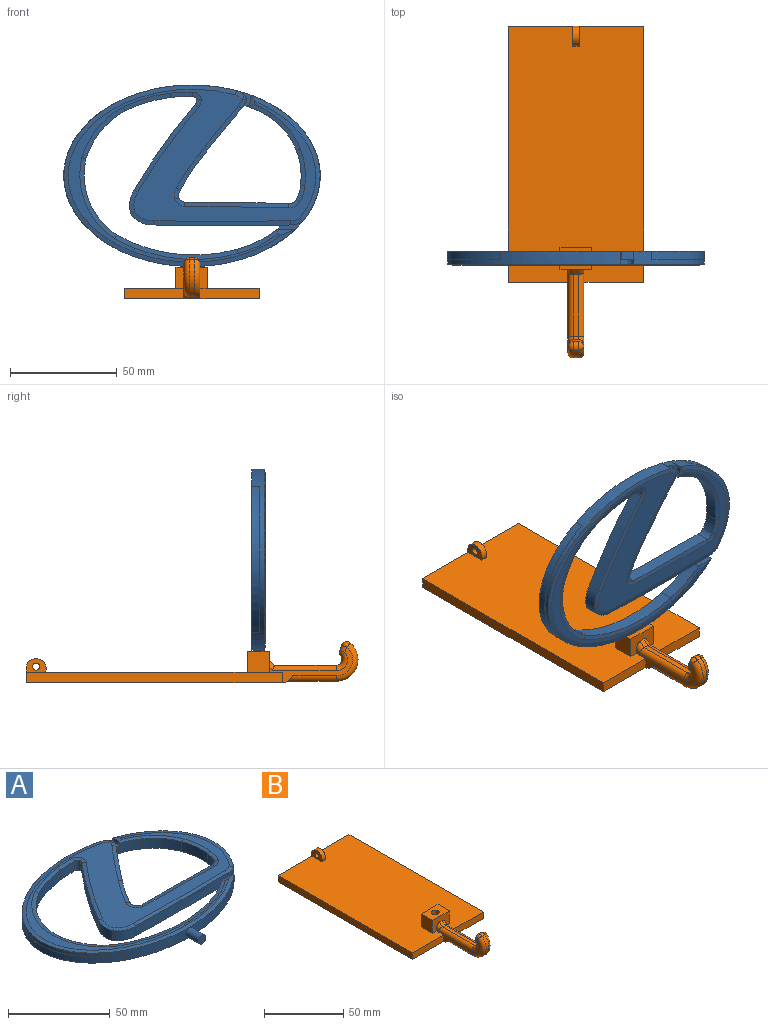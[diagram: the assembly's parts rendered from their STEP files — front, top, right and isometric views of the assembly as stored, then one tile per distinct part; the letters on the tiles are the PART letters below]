
ASSEMBLY  parts=2 mates=1
PART A: 74 faces, bbox 120.8x94.6x6.7 mm
  f0: extruded ~108.39x85.12mm, area 999.4mm2, adj f1,f4,f19,f35,f36,f37,f38,f39
  f1: plane 120.46x85.21mm, normal (0,0,-1), area 3845.7mm2, adj f0,f5,f6,f7,f8,f9,f10,f11
  f2: plane 7.37x6.32mm, normal (0,0,1), area 14.3mm2, adj f3,f17,f18,f19,f25,f34,f71
  f3: cylinder r=2.05mm len=2.18mm, axis (0,0,-1), area 3.9mm2, adj f2,f18,f19,f43
  f4: cylinder r=5144.41mm len=8.58mm, axis (0,0,-1), area 18.7mm2, adj f0,f5,f35,f40
  f5: cylinder r=52.6mm len=18.51mm, axis (0,0,-1), area 124.5mm2, adj f1,f4,f6,f42,f70
  f6: cylinder r=74.66mm len=56.61mm, axis (0,0,-1), area 350.5mm2, adj f1,f5,f7,f44
  f7: cylinder r=33.68mm len=35.7mm, axis (0,0,-1), area 245.3mm2, adj f1,f6,f8,f46
  f8: cylinder r=38.92mm len=22.56mm, axis (0,0,-1), area 178.8mm2, adj f1,f7,f9,f48
  f9: cylinder r=68.86mm len=21.32mm, axis (0,0,-1), area 133.6mm2, adj f1,f8,f10,f50
  f10: cylinder r=70.53mm len=10.22mm, axis (0,0,-1), area 61.4mm2, adj f1,f9,f11,f52
  f11: cylinder r=2.08mm len=5.99mm, axis (0,0,-1), area 17.5mm2, adj f1,f10,f20,f54
  f12: cylinder r=1264.57mm len=63.82mm, axis (0,0,-1), area 365.8mm2, adj f1,f13,f23,f35,f64,f70
  f13: cylinder r=9.39mm len=5.95mm, axis (0,0,-1), area 13.7mm2, adj f12,f24,f35,f66
  f14: cylinder r=33.54mm len=10.41mm, axis (0,0,-1), area 69.3mm2, adj f1,f15,f25,f67,f71
  f15: cylinder r=32.42mm len=15.62mm, axis (0,0,-1), area 122.6mm2, adj f1,f14,f16,f65
  f16: cylinder r=32.25mm len=16.25mm, axis (0,0,-1), area 99.2mm2, adj f1,f15,f26,f63
  f17: cylinder r=10.16mm len=5.99mm, axis (0,0,-1), area 12.1mm2, adj f1,f2,f18,f32,f47,f71
  f18: cylinder r=3.51mm len=2.18mm, axis (0,0,-1), area 3.9mm2, adj f2,f3,f17,f45
  f19: cylinder r=11.51mm len=5.99mm, axis (0,0,-1), area 10.4mm2, adj f0,f1,f2,f3,f34,f41
  f20: cylinder r=2.94mm len=5.99mm, axis (0,0,-1), area 14.2mm2, adj f1,f11,f21,f56
  f21: cylinder r=262.41mm len=39.99mm, axis (0,0,-1), area 294.8mm2, adj f1,f20,f22,f58
  f22: cylinder r=13.1mm len=11.43mm, axis (0,0,-1), area 71.6mm2, adj f1,f21,f23,f60
  f23: cylinder r=12.43mm len=10.87mm, axis (0,0,-1), area 75.2mm2, adj f1,f12,f22,f62
  f24: extruded ~59.5x33.1mm, area 204.1mm2, adj f1,f13,f25,f35,f36,f68
  f25: cylinder r=4.29mm len=5.99mm, axis (0,0,-1), area 13.8mm2, adj f1,f2,f14,f24,f34,f69
  f26: cylinder r=14.79mm len=6.9mm, axis (0,0,-1), area 43.7mm2, adj f1,f16,f27,f61
  f27: cylinder r=3.85mm len=5.99mm, axis (0,0,-1), area 24.7mm2, adj f1,f26,f28,f59
  f28: cylinder r=4569.03mm len=48.6mm, axis (0,0,-1), area 291.2mm2, adj f1,f27,f29,f57
  f29: cylinder r=3.81mm len=5.99mm, axis (0,0,-1), area 21.8mm2, adj f1,f28,f30,f55
  f30: cylinder r=4.45mm len=5.99mm, axis (0,0,-1), area 21.7mm2, adj f1,f29,f31,f53
  f31: cylinder r=112.61mm len=15.54mm, axis (0,0,-1), area 111.9mm2, adj f1,f30,f32,f51
  f32: cylinder r=421.5mm len=23.14mm, axis (0,0,-1), area 178.4mm2, adj f1,f17,f31,f49
  f33: plane 116.82x82.01mm, normal (0,0,1), area 2128.2mm2, adj f39,f40,f41,f42,f43,f44,f45,f46
  f34: extruded ~5.75x3.81mm, area 22.9mm2, adj f1,f2,f19,f25
  f35: plane 68.65x24.62mm, normal (0,0,1), area 26.9mm2, adj f0,f4,f12,f13,f24,f36,f70
  f36: extruded ~68.65x24.62mm, area 338.6mm2, adj f0,f1,f24,f35
  f37: plane 68.65x24.62mm, normal (0,0,1), area 5.9mm2, adj f0,f38
  f38: extruded ~68.65x24.62mm, area 338.6mm2, adj f0,f1,f37
  f39: bspline ~112.84x85.26mm, area 472.9mm2, adj f0,f33,f40,f41
  f40: cone r=5142.38mm half-angle=80deg, axis (0,0,-1), area 11.3mm2, adj f4,f33,f39,f42
  f41: cone r=9.48mm half-angle=80deg, axis (0,0,-1), area 8.4mm2, adj f19,f33,f39,f43
  f42: cone r=52.6mm half-angle=80deg, axis (0,0,1), area 43mm2, adj f5,f33,f40,f44
  f43: cone r=0.02mm half-angle=80deg, axis (0,0,-1), area 1.9mm2, adj f3,f33,f41,f45
  f44: cone r=74.66mm half-angle=80deg, axis (0,0,1), area 122.4mm2, adj f6,f33,f42,f46
  f45: cone r=1.48mm half-angle=80deg, axis (0,0,-1), area 2.5mm2, adj f18,f33,f43,f47
  f46: cone r=33.68mm half-angle=80deg, axis (0,0,1), area 87.2mm2, adj f7,f33,f44,f48
  f47: cone r=8.12mm half-angle=80deg, axis (0,0,-1), area 5.6mm2, adj f17,f33,f45,f49
  f48: cone r=38.92mm half-angle=80deg, axis (0,0,1), area 63.3mm2, adj f8,f33,f46,f50
  f49: cone r=421.5mm half-angle=80deg, axis (0,0,1), area 61.6mm2, adj f32,f33,f47,f51
  f50: cone r=68.86mm half-angle=80deg, axis (0,0,1), area 46.8mm2, adj f9,f33,f48,f52
  f51: cone r=112.61mm half-angle=80deg, axis (0,0,1), area 38.8mm2, adj f31,f33,f49,f53
  f52: cone r=70.53mm half-angle=80deg, axis (0,0,1), area 21.4mm2, adj f10,f33,f50,f54
  f53: cone r=4.45mm half-angle=80deg, axis (0,0,1), area 9.3mm2, adj f30,f33,f51,f55
  f54: cone r=2.08mm half-angle=80deg, axis (0,0,1), area 9.1mm2, adj f11,f33,f52,f56
  f55: cone r=3.81mm half-angle=80deg, axis (0,0,1), area 9.9mm2, adj f29,f33,f53,f57
  f56: cone r=2.94mm half-angle=80deg, axis (0,0,1), area 6.7mm2, adj f20,f33,f54,f58
  f57: cone r=4567mm half-angle=80deg, axis (0,0,-1), area 100.3mm2, adj f28,f33,f55,f59
  f58: cone r=260.38mm half-angle=80deg, axis (0,0,-1), area 101.1mm2, adj f21,f33,f56,f60
  f59: cone r=3.85mm half-angle=80deg, axis (0,0,1), area 10.7mm2, adj f27,f33,f57,f61
  f60: cone r=11.07mm half-angle=80deg, axis (0,0,-1), area 22.5mm2, adj f22,f33,f58,f62
  f61: cone r=14.79mm half-angle=80deg, axis (0,0,1), area 16mm2, adj f26,f33,f59,f63
  f62: cone r=10.4mm half-angle=80deg, axis (0,0,-1), area 23.5mm2, adj f23,f33,f60,f64
  f63: cone r=32.25mm half-angle=80deg, axis (0,0,1), area 35.1mm2, adj f16,f33,f61,f65
  f64: cone r=1262.54mm half-angle=80deg, axis (0,0,-1), area 131.8mm2, adj f12,f33,f62,f66
  f65: cone r=32.42mm half-angle=80deg, axis (0,0,1), area 43.5mm2, adj f15,f33,f63,f67
  f66: cone r=7.36mm half-angle=80deg, axis (0,0,-1), area 11.4mm2, adj f13,f33,f64,f68
  f67: cone r=33.54mm half-angle=80deg, axis (0,0,1), area 21.6mm2, adj f14,f33,f65,f69
  f68: bspline ~63.5x37.27mm, area 151.3mm2, adj f24,f33,f66,f69
  f69: cone r=4.29mm half-angle=80deg, axis (0,0,1), area 8.9mm2, adj f25,f33,f67,f68
  f70: cylinder r=12.26mm len=3.81mm, axis (0,0,-1), area 11.1mm2, adj f1,f5,f12,f35
  f71: cylinder r=31.63mm len=3.81mm, axis (0,0,-1), area 5.8mm2, adj f1,f2,f14,f17
  f72: cylinder r=2.48mm len=8.96mm, axis (0,1,0), area 139.3mm2, adj f0,f73
  f73: plane 4.95x4.95mm, normal (0,-1,0), area 19.2mm2, adj f72
PART B: 45 faces, bbox 63.5x156.6x19.5 mm
  f0: plane 28x5mm, normal (0,-1,0), area 140mm2, adj f2,f3,f7,f14
  f1: plane 15x10mm, normal (0,-1,0), area 110.6mm2, adj f2,f8,f10,f12,f14,f16,f21,f24
  f2: plane 120x63.5mm, normal (0,0,1), area 7395.8mm2, adj f0,f1,f3,f4,f5,f6,f8,f9
  f3: plane 120x5mm, normal (1,0,0), area 600mm2, adj f0,f2,f4,f7
  f4: plane 63.5x5mm, normal (0,1,0), area 317.5mm2, adj f2,f3,f5,f7
  f5: plane 120x5mm, normal (-1,0,0), area 600mm2, adj f2,f4,f6,f7
  f6: plane 28x5mm, normal (0,-1,0), area 140mm2, adj f2,f5,f7,f16
  f7: plane 121.8x63.5mm, normal (0,0,-1), area 7633.5mm2, adj f0,f3,f4,f5,f6,f14,f16,f22
  f8: plane 10x10mm, normal (1,0,0), area 100mm2, adj f1,f2,f9,f12
  f9: plane 15x10mm, normal (0,1,0), area 150mm2, adj f2,f8,f10,f12
  f10: plane 10x10mm, normal (-1,0,0), area 100mm2, adj f1,f2,f9,f12
  f11: cylinder r=2.5mm len=10mm, axis (0,0,-1), area 157.1mm2, adj f12,f13
  f12: plane 15x10mm, normal (0,0,1), area 130.4mm2, adj f1,f8,f9,f10,f11
  f13: plane 5x5mm, normal (0,0,1), area 19.6mm2, adj f11
  f14: plane 39.18x16.8mm, normal (1,0,0), area 115.2mm2, adj f0,f1,f2,f7,f22,f23,f24,f25
  f15: plane 28.98x2.42mm, normal (0,0,1), area 70.1mm2, adj f19,f21,f26,f38
  f16: plane 39.18x16.8mm, normal (-1,0,0), area 115.2mm2, adj f1,f2,f6,f7,f22,f28,f32,f35
  f17: plane 2.47x2.42mm, normal (0,0.94,0.35), area 6.4mm2, adj f30,f31,f36,f37
  f18: plane 22.86x2.42mm, normal (0,0,-1), area 55.3mm2, adj f20,f22,f23,f28
  f19: cylinder r=2.7mm len=4.45mm, axis (-1,0,0), area 14.9mm2, adj f15,f29,f36,f40
  f20: cylinder r=10.2mm len=18.01mm, axis (-1,0,0), area 60.3mm2, adj f18,f25,f31,f32
  f21: plane 2.54x2.54mm, normal (0,-0.71,0.71), area 8.7mm2, adj f1,f15,f24,f35
  f22: plane 7.5x3.28mm, normal (0,-0.71,-0.71), area 11.7mm2, adj f7,f14,f16,f18,f23,f28
  f23: cylinder r=2.54mm len=22.86mm, axis (0,1,0), area 87.5mm2, adj f14,f18,f22,f25
  f24: cylinder r=2.54mm len=5.08mm, axis (0,0.71,0.71), area 12.2mm2, adj f1,f14,f21,f26
  f25: torus R=7.66mm, axis (-1,0,0), area 90.4mm2, adj f14,f20,f23,f27
  f26: cylinder r=2.54mm len=30.03mm, axis (0,1,0), area 117.1mm2, adj f14,f15,f24,f29
  f27: sphere r=2.54mm, area 12.3mm2, adj f25,f30,f31
  f28: cylinder r=2.54mm len=22.86mm, axis (0,-1,0), area 87.5mm2, adj f16,f18,f22,f32
  f29: torus R=5.24mm, axis (-1,0,0), area 32.9mm2, adj f14,f19,f26,f33
  f30: cylinder r=2.54mm len=3.37mm, axis (0,-0.35,0.94), area 10.5mm2, adj f14,f17,f27,f33
  f31: cylinder r=2.54mm len=4.01mm, axis (-1,0,0), area 11.7mm2, adj f17,f20,f27,f34
  f32: torus R=7.66mm, axis (-1,0,0), area 90.4mm2, adj f16,f20,f28,f34
  f33: sphere r=2.54mm, area 6.9mm2, adj f29,f30,f36
  f34: sphere r=2.54mm, area 12.3mm2, adj f31,f32,f37
  f35: cylinder r=2.54mm len=5.08mm, axis (0,0.71,0.71), area 12.2mm2, adj f1,f16,f21,f38
  f36: cylinder r=2.54mm len=2.54mm, axis (-1,0,0), area 6.5mm2, adj f17,f19,f33,f39
  f37: cylinder r=2.54mm len=3.37mm, axis (0,-0.35,0.94), area 10.5mm2, adj f16,f17,f34,f39
  f38: cylinder r=2.54mm len=30.03mm, axis (0,-1,0), area 117.1mm2, adj f15,f16,f35,f40
  f39: sphere r=2.54mm, area 6.9mm2, adj f36,f37,f40
  f40: torus R=5.24mm, axis (-1,0,0), area 32.9mm2, adj f16,f19,f38,f39
  f41: cylinder r=1.63mm len=3.26mm, axis (-1,0,0), area 32.5mm2, adj f43,f44
  f42: cylinder r=4.75mm len=9.5mm, axis (-1,0,0), area 58.1mm2, adj f2,f43,f44
  f43: plane 9.5x6.4mm, normal (1,0,0), area 42.5mm2, adj f2,f41,f42
  f44: plane 9.5x6.4mm, normal (-1,0,0), area 42.5mm2, adj f2,f41,f42
PLACE A rot(axis=(1,0,0),90deg) t=(-4.27,-45.74,41.68)mm
PLACE B at identity
MATE fastened A.f72 <-> B.f11  axis (0,0,-1) through (0,-48.88,6.27)mm
